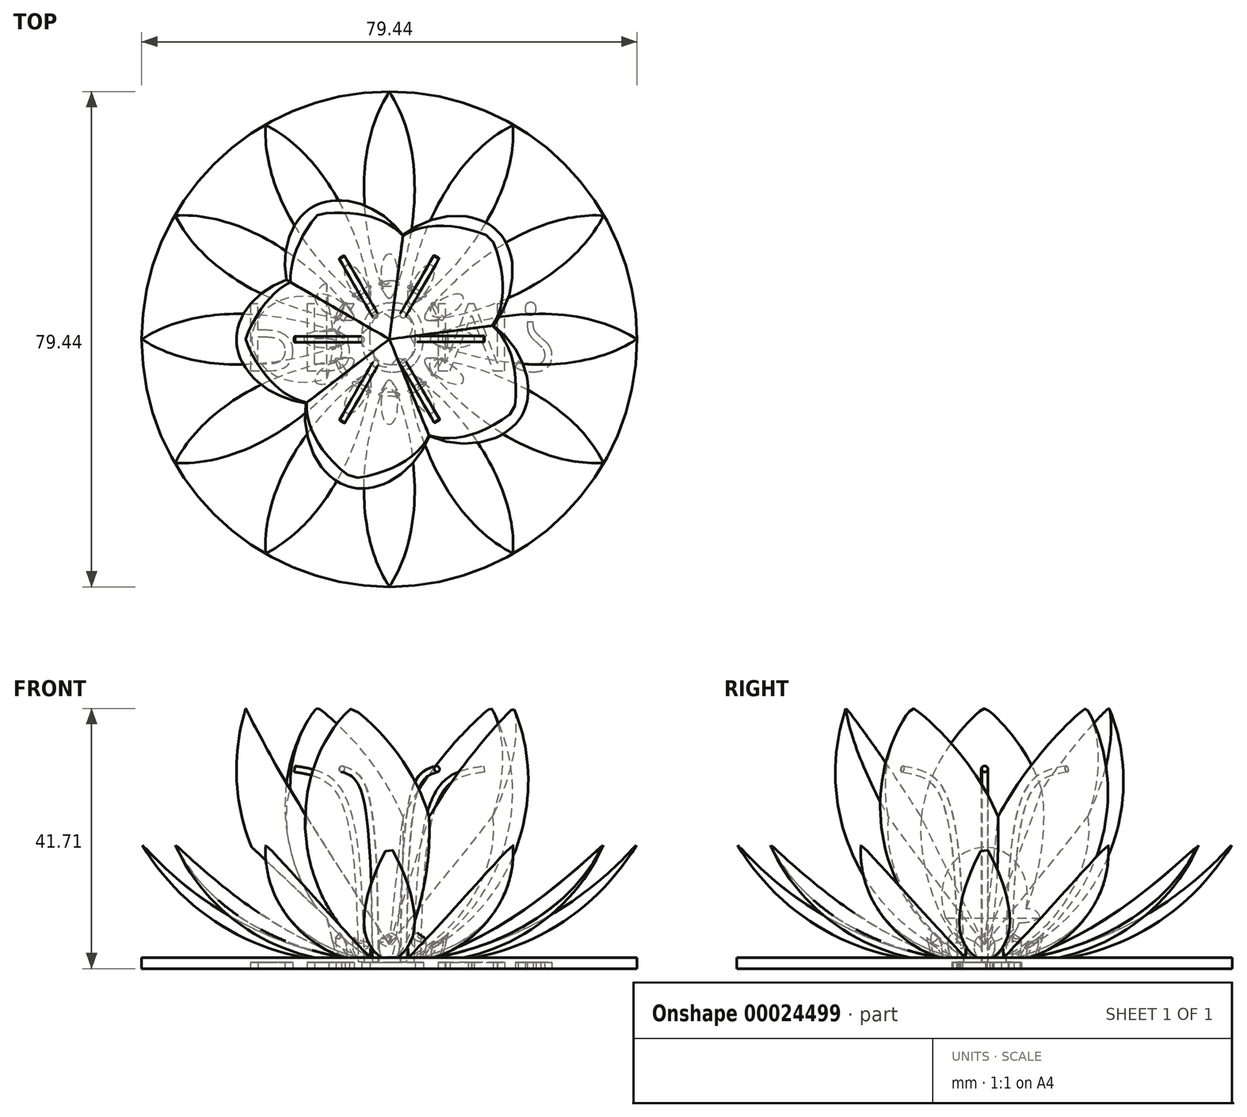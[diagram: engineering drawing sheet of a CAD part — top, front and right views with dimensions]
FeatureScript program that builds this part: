
annotation { "Feature Type Name" : "Feature", "Feature Type Description" : "" }
export const myFeature = defineFeature(function(context is Context, id is Id, definition is map)
    precondition{}
    {
        {
            var Q0;
            Q0=qCreatedBy(makeId("Front.planeOp"),FACE);
            var sketch = newSketch(context, id + "F0", { "sketchPlane" : qUnion([Q0])});
            skArc(sketch, "E0", {"start": v(-22.86, 41.91) * mm, "mid": v(-18.74, 16.97) * mm, "end": v(0, 0) * mm});
            skArc(sketch, "E1", {"start": v(0, 0) * mm, "mid": v(-2.33, 25.92) * mm, "end": v(-22.86, 41.91) * mm});
            skLineSegment(sketch, "E2", {"start": v(-22.86, 41.91) * mm, "end": v(0, 0) * mm});
            skSolve(sketch);
        }
        {
            var Q0;
            Q0=makeQuery(id+"F0.imprint","IMPRINT",FACE,{"disambiguationData":[TD([[makeQuery(id+"F0.imprint","IMPRINT",EDGE,{"derivedFrom":sQuery(id+"F0.wireOp",EDGE,"E1")}),1.0]])]});
            var Q1;
            Q1=sQuery(id+"F0.wireOp",EDGE,"E2");
            revolve(context, id + "F1", {"entities" : qUnion([Q0]), "axis" : qUnion([Q1]), "revolveType" : RevolveType.FULL});
        }
        {
            var Q0;
            Q0=qCreatedBy(makeId("Front.planeOp"),FACE);
            var sketch = newSketch(context, id + "F2", { "sketchPlane" : qUnion([Q0])});
            skFitSpline(sketch, "E3", {"points": [v(-29.04, 63.58) * mm, v(7.35, -8.37) * mm, v(15.22, -26.5) * mm], "startDerivative": vector(-11.27, -79.75) * mm, "endDerivative": vector(57.22, -91.86) * mm});
            skLineSegment(sketch, "E4", {"start": v(-29.04, 63.58) * mm, "end": v(49.38, 6.86) * mm});
            skLineSegment(sketch, "E5", {"start": v(15.22, -26.5) * mm, "end": v(49.38, 6.86) * mm});
            skSolve(sketch);
        }
        {
            var Q0;
            Q0=makeQuery(id+"F2.imprint","IMPRINT",FACE,{"disambiguationData":[TD([[makeQuery(id+"F2.imprint","IMPRINT",EDGE,{"derivedFrom":sQuery(id+"F2.wireOp",EDGE,"E3")}),1.0]])]});
            extrude(context, id + "F3", {"entities" : qUnion([Q0]), "operationType" : NewBodyOperationType.REMOVE, "depth" : 304.8 * mm, "hasSecondDirection" : true, "secondDirectionOppositeDirection" : true, "secondDirectionDepth" : 25.4 * mm});
        }
        {
            var Q0;
            Q0=qCreatedBy(makeId("Top.planeOp"),FACE);
            var sketch = newSketch(context, id + "F4", { "sketchPlane" : qUnion([Q0])});
            skCircle(sketch, "E6", {"center": v(0, 0) * mm, "radius": 12.08 * mm});
            skSolve(sketch);
        }
        {
            var Q0;
            Q0=makeQuery(id+"F1.opRevolve","SWEPT_BODY",BODY,{"disambiguationData":[OSD([sQuery(id+"F0.wireOp",EDGE,"E1"),sQuery(id+"F0.wireOp",EDGE,"E2")])]});
            var Q1;
            Q1=sQuery(id+"F4.wireOp",EDGE,"E6");
            circularPattern(context, id + "F5", {"operationType" : NewBodyOperationType.ADD, "entities" : qUnion([Q0]), "axis" : qUnion([Q1]), "angle" : 75 * degree, "instanceCount" : 5});
        }
        {
            var Q0;
            Q0=qCreatedBy(makeId("Top.planeOp"),FACE);
            var sketch = newSketch(context, id + "F6", { "sketchPlane" : qUnion([Q0])});
            skCircle(sketch, "E7", {"center": v(0, 0) * mm, "radius": 39.72 * mm});
            skSolve(sketch);
        }
        {
            var Q0;
            Q0 = qSketchRegion(id + "F6", true);
            extrude(context, id + "F7", {"entities" : qUnion([Q0]), "oppositeDirection" : true, "depth" : 0.25 * mm, "hasSecondDirection" : true, "secondDirectionOppositeDirection" : false, "secondDirectionDepth" : 1.52 * mm});
        }
        {
            var Q0;
            Q0=qCreatedBy(makeId("Front.planeOp"),FACE);
            var sketch = newSketch(context, id + "F8", { "sketchPlane" : qUnion([Q0])});
            skArc(sketch, "E8", {"start": v(-39.63, 19.56) * mm, "mid": v(-25.39, 5.76) * mm, "end": v(-6.17, 0.87) * mm});
            skArc(sketch, "E9", {"start": v(-6.17, 0.87) * mm, "mid": v(-21.24, 13.19) * mm, "end": v(-39.63, 19.56) * mm});
            skLineSegment(sketch, "E10", {"start": v(-39.63, 19.56) * mm, "end": v(-6.17, 0.87) * mm});
            skSolve(sketch);
        }
        {
            var Q0;
            Q0=makeQuery(id+"F8.imprint","IMPRINT",FACE,{"disambiguationData":[TD([[makeQuery(id+"F8.imprint","IMPRINT",EDGE,{"derivedFrom":sQuery(id+"F8.wireOp",EDGE,"E8")}),1.0]])]});
            var Q1;
            Q1=sQuery(id+"F8.wireOp",EDGE,"E10");
            revolve(context, id + "F9", {"entities" : qUnion([Q0]), "axis" : qUnion([Q1]), "revolveType" : RevolveType.FULL});
        }
        {
            var Q0;
            Q0=qCreatedBy(makeId("Front.planeOp"),FACE);
            var sketch = newSketch(context, id + "F10", { "sketchPlane" : qUnion([Q0])});
            skArc(sketch, "E11", {"start": v(-42.38, 22.98) * mm, "mid": v(-27.36, 9.26) * mm, "end": v(-8.5, 1.62) * mm});
            skLineSegment(sketch, "E12", {"start": v(-42.38, 22.98) * mm, "end": v(-22.7, 19.8) * mm});
            skLineSegment(sketch, "E13", {"start": v(-22.7, 19.8) * mm, "end": v(-10.01, 7.88) * mm});
            skLineSegment(sketch, "E14", {"start": v(-10.01, 7.88) * mm, "end": v(-8.5, 1.62) * mm});
            skSolve(sketch);
        }
        {
            var Q0;
            Q0 = qSketchRegion(id + "F10", true);
            extrude(context, id + "F11", {"entities" : qUnion([Q0]), "operationType" : NewBodyOperationType.REMOVE, "depth" : 304.8 * mm, "hasSecondDirection" : true, "secondDirectionOppositeDirection" : true, "secondDirectionDepth" : 25.4 * mm});
        }
        {
            var Q0;
            Q0=makeQuery(id+"F9.opRevolve","SWEPT_BODY",BODY,{"disambiguationData":[OSD([sQuery(id+"F8.wireOp",EDGE,"E8"),sQuery(id+"F8.wireOp",EDGE,"E10")])]});
            var Q1;
            Q1=makeQuery(id+"F7.opExtrude","CAP_EDGE",EDGE,{"disambiguationData":[OSD([sQuery(id+"F6.wireOp",EDGE,"E7")])],"isStart":true});
            circularPattern(context, id + "F12", {"operationType" : NewBodyOperationType.ADD, "entities" : qUnion([Q0]), "axis" : qUnion([Q1]), "angle" : 30 * degree, "instanceCount" : 12});
        }
        {
            var Q0;
            Q0=qCreatedBy(makeId("Front.planeOp"),FACE);
            var sketch = newSketch(context, id + "F13", { "sketchPlane" : qUnion([Q0])});
            skFitSpline(sketch, "E15", {"points": [v(-15.18, 31.82) * mm, v(-8.34, 28.74) * mm, v(-4.42, 0.79) * mm], "startDerivative": vector(22.52, -3.4) * mm, "endDerivative": vector(1.27, -53.34) * mm});
            skSolve(sketch);
        }
        {
            var Q0;
            Q0=makeQuery(id+"F7.opExtrude","CAP_FACE",FACE,{"disambiguationData":[OSD([sQuery(id+"F6.wireOp",EDGE,"E7")])],"isStart":true});
            var sketch = newSketch(context, id + "F14", { "sketchPlane" : qUnion([Q0])});
            skCircle(sketch, "E16", {"center": v(-4.5, -0.04) * mm, "radius": 0.49 * mm});
            skSolve(sketch);
        }
        {
            var Q0;
            Q0 = qSketchRegion(id + "F14", true);
            var Q1;
            Q1 = qConstructionFilter(qBodyType(qCreatedBy(id + "F13" ,EDGE), BodyType.WIRE), ConstructionObject.NO);
            sweep(context, id + "F15", {"profiles" : qUnion([Q0]), "path" : qUnion([Q1])});
        }
        {
            var Q0;
            Q0=makeQuery(id+"F15.opSweep","SWEPT_BODY",BODY,{"disambiguationData":[OSD([sQuery(id+"F13.wireOp",EDGE,"E15"),sQuery(id+"F14.wireOp",EDGE,"E16")])]});
            var Q1;
            Q1=makeQuery(id+"F7.opExtrude","CAP_EDGE",EDGE,{"disambiguationData":[OSD([sQuery(id+"F6.wireOp",EDGE,"E7")])],"isStart":true});
            circularPattern(context, id + "F16", {"entities" : qUnion([Q0]), "axis" : qUnion([Q1]), "angle" : 60 * degree, "instanceCount" : 6});
        }
        {
            var Q0;
            Q0=makeQuery(id+"F7.opExtrude","CAP_FACE",FACE,{"disambiguationData":[OSD([sQuery(id+"F6.wireOp",EDGE,"E7")])],"isStart":false});
            var sketch = newSketch(context, id + "F17", { "sketchPlane" : qUnion([Q0])});
            skSolve(sketch);
        }
        {
            var Q0;
            Q0=makeQuery(id+"F17.imprint","IMPRINT",FACE,{"disambiguationData":[TD([[makeQuery(id+"F17.imprint","IMPRINT",EDGE,{"derivedFrom":makeQuery(id+"F7.opExtrude","CAP_EDGE",EDGE,{"disambiguationData":[OSD([sQuery(id+"F6.wireOp",EDGE,"E7")])],"isStart":false})}),-1.0]])]});
            var sketch = newSketch(context, id + "F18", { "sketchPlane" : qUnion([Q0])});
            skText(sketch, "E17", { "text": "PROM?", "fontName": "OpenSans-Regular.ttf"});
            const initialGuessF18  = {"E17": [-0.02377, -0.00568, 1, 0, 0.01086]};
            skSetInitialGuess(sketch, initialGuessF18);
            skSolve(sketch);
        }
        {
            var Q0;
            Q0 = qSketchRegion(id + "F18", true);
            extrude(context, id + "F19", {"entities" : qUnion([Q0]), "operationType" : NewBodyOperationType.REMOVE, "oppositeDirection" : true, "depth" : 1.02 * mm});
        }
    });
